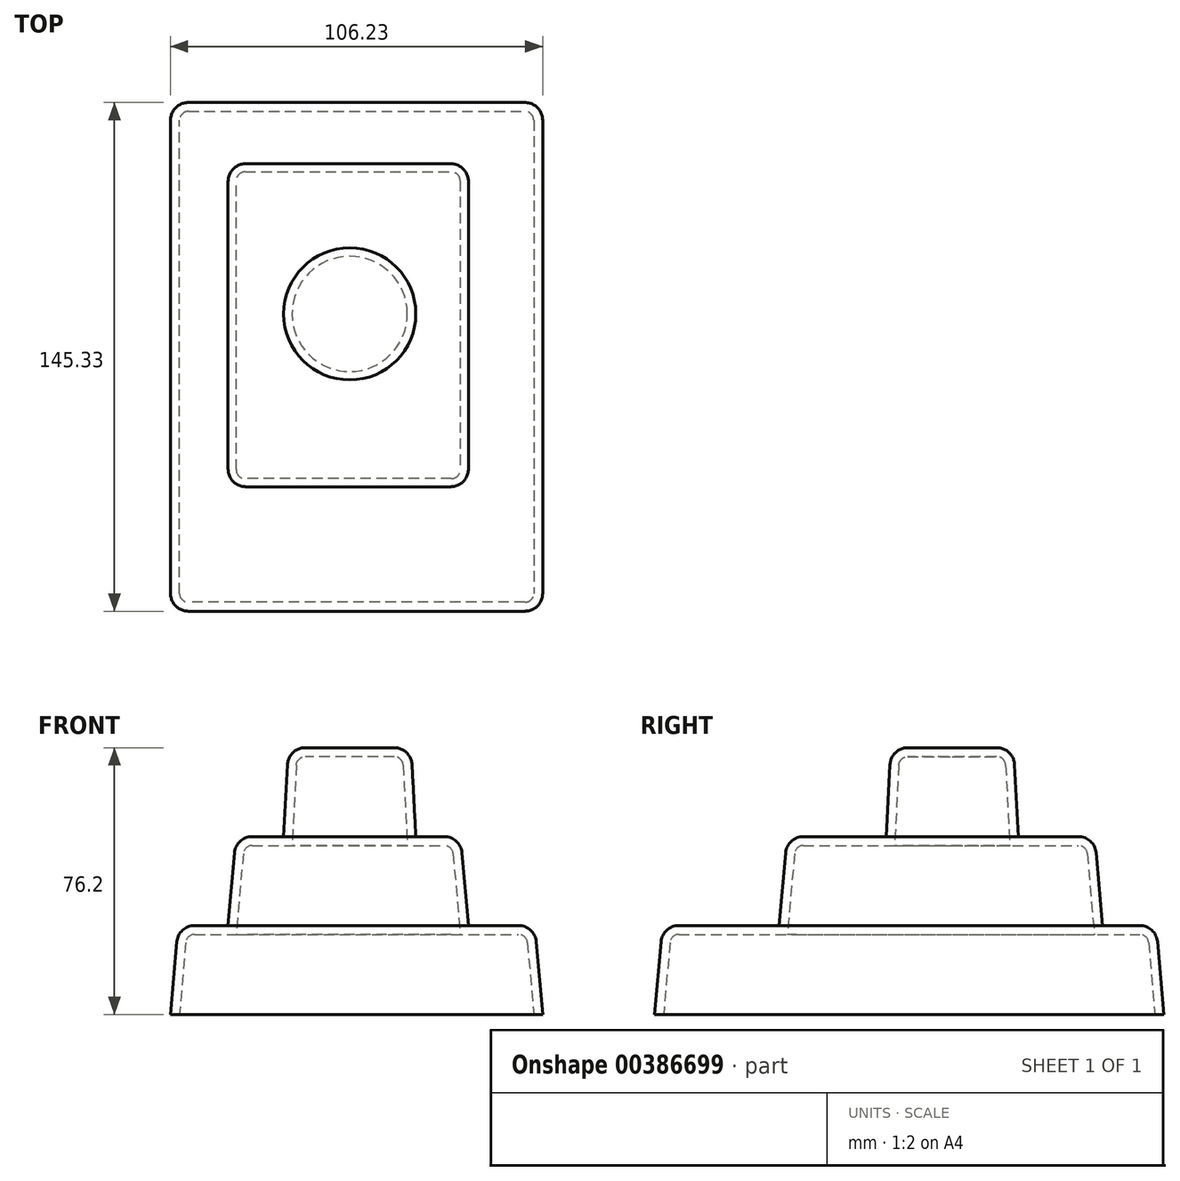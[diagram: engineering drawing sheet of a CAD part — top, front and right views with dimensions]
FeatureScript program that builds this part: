
annotation { "Feature Type Name" : "Feature", "Feature Type Description" : "" }
export const myFeature = defineFeature(function(context is Context, id is Id, definition is map)
    precondition{}
    {
        {
            var Q0;
            Q0=qCreatedBy(makeId("Top.planeOp"),FACE);
            var sketch = newSketch(context, id + "F0", { "sketchPlane" : qUnion([Q0])});
            skLineSegment(sketch, "E0.bottom", {"start": v(-63.37, -74.92) * mm, "end": v(42.86, -74.92) * mm});
            skLineSegment(sketch, "E0.top", {"start": v(-63.37, 70.41) * mm, "end": v(42.86, 70.41) * mm});
            skLineSegment(sketch, "E0.left", {"start": v(-63.37, -74.92) * mm, "end": v(-63.37, 70.41) * mm});
            skLineSegment(sketch, "E0.right", {"start": v(42.86, -74.92) * mm, "end": v(42.86, 70.41) * mm});
            skSolve(sketch);
        }
        {
            var Q0;
            Q0 = qSketchRegion(id + "F0", true);
            extrude(context, id + "F1", {"entities" : qUnion([Q0]), "depth" : 25.4 * mm, "hasDraft" : true, "draftAngle" : 5 * degree, "draftPullDirection" : true});
        }
        {
            var Q0;
            Q0=makeQuery(id+"F1.opExtrude","CAP_FACE",FACE,{"disambiguationData":[OSD([sQuery(id+"F0.wireOp",EDGE,"E0.bottom"),sQuery(id+"F0.wireOp",EDGE,"E0.top"),sQuery(id+"F0.wireOp",EDGE,"E0.left"),sQuery(id+"F0.wireOp",EDGE,"E0.right"),sQuery(id+"F0.wireOp",EDGE,"h4BqIlvT-tDls-YcwB-oSV5-vmF0mrKVJpqu.bottom"),sQuery(id+"F0.wireOp",EDGE,"h4BqIlvT-tDls-YcwB-oSV5-vmF0mrKVJpqu.top"),sQuery(id+"F0.wireOp",EDGE,"h4BqIlvT-tDls-YcwB-oSV5-vmF0mrKVJpqu.left"),sQuery(id+"F0.wireOp",EDGE,"h4BqIlvT-tDls-YcwB-oSV5-vmF0mrKVJpqu.right")])],"isStart":false});
            var sketch = newSketch(context, id + "F2", { "sketchPlane" : qUnion([Q0])});
            skLineSegment(sketch, "E1.bottom", {"start": v(-46.94, 52.91) * mm, "end": v(21.66, 52.91) * mm});
            skLineSegment(sketch, "E1.top", {"start": v(-46.94, -39.37) * mm, "end": v(21.66, -39.37) * mm});
            skLineSegment(sketch, "E1.left", {"start": v(-46.94, 52.91) * mm, "end": v(-46.94, -39.37) * mm});
            skLineSegment(sketch, "E1.right", {"start": v(21.66, 52.91) * mm, "end": v(21.66, -39.37) * mm});
            skSolve(sketch);
        }
        {
            var Q0;
            Q0 = qSketchRegion(id + "F2", true);
            var Q1;
            Q1 = qConstructionFilter(qBodyType(qCreatedBy(id + "F2" ,EDGE), BodyType.WIRE), ConstructionObject.NO);
            extrude(context, id + "F3", {"entities" : qUnion([Q0]), "operationType" : NewBodyOperationType.ADD, "surfaceEntities" : qUnion([Q1]), "depth" : 25.4 * mm, "hasDraft" : true, "draftAngle" : 5 * degree, "draftPullDirection" : true});
        }
        {
            var Q0;
            Q0=makeQuery(id+"F3.opExtrude","CAP_EDGE",EDGE,{"disambiguationData":[OSD([sQuery(id+"F2.wireOp",EDGE,"E1.right")])],"isStart":true});
            var Q1;
            Q1=makeQuery(id+"F3.opExtrude","CAP_EDGE",EDGE,{"disambiguationData":[OSD([sQuery(id+"F2.wireOp",EDGE,"E1.bottom")])],"isStart":true});
            var Q2;
            Q2=makeQuery(id+"F3.opExtrude","CAP_EDGE",EDGE,{"disambiguationData":[OSD([sQuery(id+"F2.wireOp",EDGE,"E1.left")])],"isStart":true});
            var Q3;
            Q3=makeQuery(id+"F3.opExtrude","CAP_EDGE",EDGE,{"disambiguationData":[OSD([sQuery(id+"F2.wireOp",EDGE,"E1.top")])],"isStart":true});
            var Q4;
            Q4=makeQuery(id+"F3.opExtrude","SWEPT_EDGE",EDGE,{"disambiguationData":[OSD([sQuery(id+"F2.wireOp",EDGE,"E1.top"),sQuery(id+"F2.wireOp",EDGE,"E1.left")])]});
            var Q5;
            Q5=makeQuery(id+"F3.opExtrude","SWEPT_EDGE",EDGE,{"disambiguationData":[OSD([sQuery(id+"F2.wireOp",EDGE,"E1.top"),sQuery(id+"F2.wireOp",EDGE,"E1.right")])]});
            var Q6;
            Q6=makeQuery(id+"F3.opExtrude","SWEPT_EDGE",EDGE,{"disambiguationData":[OSD([sQuery(id+"F2.wireOp",EDGE,"E1.bottom"),sQuery(id+"F2.wireOp",EDGE,"E1.left")])]});
            var Q7;
            Q7=makeQuery(id+"F3.opExtrude","SWEPT_EDGE",EDGE,{"disambiguationData":[OSD([sQuery(id+"F2.wireOp",EDGE,"E1.bottom"),sQuery(id+"F2.wireOp",EDGE,"E1.right")])]});
            fillet(context, id + "F4", {"entities" : qUnion([Q0, Q1, Q2, Q3, Q4, Q5, Q6, Q7]), "radius" : 5.08 * mm, "tangentPropagation" : true, "allowEdgeOverflow" : false});
        }
        {
            var Q0;
            Q0=makeQuery(id+"F3.opExtrude","CAP_FACE",FACE,{"disambiguationData":[OSD([sQuery(id+"F2.wireOp",EDGE,"E1.bottom"),sQuery(id+"F2.wireOp",EDGE,"E1.top"),sQuery(id+"F2.wireOp",EDGE,"E1.left"),sQuery(id+"F2.wireOp",EDGE,"E1.right")])],"isStart":false});
            var sketch = newSketch(context, id + "F5", { "sketchPlane" : qUnion([Q0])});
            skCircle(sketch, "E2", {"center": v(-12.2, 10.02) * mm, "radius": 18.86 * mm});
            skSolve(sketch);
        }
        {
            var Q0;
            Q0 = qSketchRegion(id + "F5", true);
            extrude(context, id + "F6", {"entities" : qUnion([Q0]), "operationType" : NewBodyOperationType.ADD, "depth" : 25.4 * mm, "hasDraft" : true, "draftAngle" : 3 * degree, "draftPullDirection" : true});
        }
        {
            var Q0;
            Q0=makeQuery(id+"F6.opExtrude","CAP_EDGE",EDGE,{"disambiguationData":[OSD([sQuery(id+"F5.wireOp",EDGE,"E2")])],"isStart":true});
            var Q1;
            Q1=makeQuery(id+"F3.opExtrude","CAP_EDGE",EDGE,{"disambiguationData":[OSD([sQuery(id+"F2.wireOp",EDGE,"E1.right")])],"isStart":false});
            fillet(context, id + "F7", {"entities" : qUnion([Q0, Q1]), "radius" : 5.08 * mm, "tangentPropagation" : true, "allowEdgeOverflow" : false});
        }
        {
            var Q0;
            Q0=makeQuery(id+"F6.opExtrude","CAP_EDGE",EDGE,{"disambiguationData":[OSD([sQuery(id+"F5.wireOp",EDGE,"E2")])],"isStart":false});
            fillet(context, id + "F8", {"entities" : qUnion([Q0]), "radius" : 5.08 * mm, "tangentPropagation" : true, "allowEdgeOverflow" : false});
        }
        {
            var Q0;
            Q0=makeQuery(id+"F1.opExtrude","SWEPT_EDGE",EDGE,{"disambiguationData":[OSD([sQuery(id+"F0.wireOp",EDGE,"E0.bottom"),sQuery(id+"F0.wireOp",EDGE,"E0.right")])]});
            var Q1;
            Q1=makeQuery(id+"F1.opExtrude","CAP_EDGE",EDGE,{"disambiguationData":[OSD([sQuery(id+"F0.wireOp",EDGE,"E0.bottom")])],"isStart":false});
            var Q2;
            Q2=makeQuery(id+"F1.opExtrude","CAP_EDGE",EDGE,{"disambiguationData":[OSD([sQuery(id+"F0.wireOp",EDGE,"E0.right")])],"isStart":false});
            var Q3;
            Q3=makeQuery(id+"F1.opExtrude","SWEPT_EDGE",EDGE,{"disambiguationData":[OSD([sQuery(id+"F0.wireOp",EDGE,"E0.bottom"),sQuery(id+"F0.wireOp",EDGE,"E0.left")])]});
            var Q4;
            Q4=makeQuery(id+"F1.opExtrude","SWEPT_EDGE",EDGE,{"disambiguationData":[OSD([sQuery(id+"F0.wireOp",EDGE,"E0.top"),sQuery(id+"F0.wireOp",EDGE,"E0.right")])]});
            var Q5;
            Q5=makeQuery(id+"F1.opExtrude","CAP_EDGE",EDGE,{"disambiguationData":[OSD([sQuery(id+"F0.wireOp",EDGE,"E0.top")])],"isStart":false});
            var Q6;
            Q6=makeQuery(id+"F1.opExtrude","SWEPT_EDGE",EDGE,{"disambiguationData":[OSD([sQuery(id+"F0.wireOp",EDGE,"E0.top"),sQuery(id+"F0.wireOp",EDGE,"E0.left")])]});
            var Q7;
            Q7=makeQuery(id+"F1.opExtrude","CAP_EDGE",EDGE,{"disambiguationData":[OSD([sQuery(id+"F0.wireOp",EDGE,"E0.left")])],"isStart":false});
            fillet(context, id + "F9", {"entities" : qUnion([Q0, Q1, Q2, Q3, Q4, Q5, Q6, Q7]), "radius" : 5.08 * mm, "tangentPropagation" : true, "allowEdgeOverflow" : false});
        }
        {
            var Q0;
            Q0=makeQuery(id+"F1.opExtrude","CAP_FACE",FACE,{"disambiguationData":[OSD([sQuery(id+"F0.wireOp",EDGE,"E0.bottom"),sQuery(id+"F0.wireOp",EDGE,"E0.top"),sQuery(id+"F0.wireOp",EDGE,"E0.left"),sQuery(id+"F0.wireOp",EDGE,"E0.right")])],"isStart":true});
            shell(context, id + "F10", {"entities" : qUnion([Q0]), "thickness" : 2.54 * mm});
        }
    });
